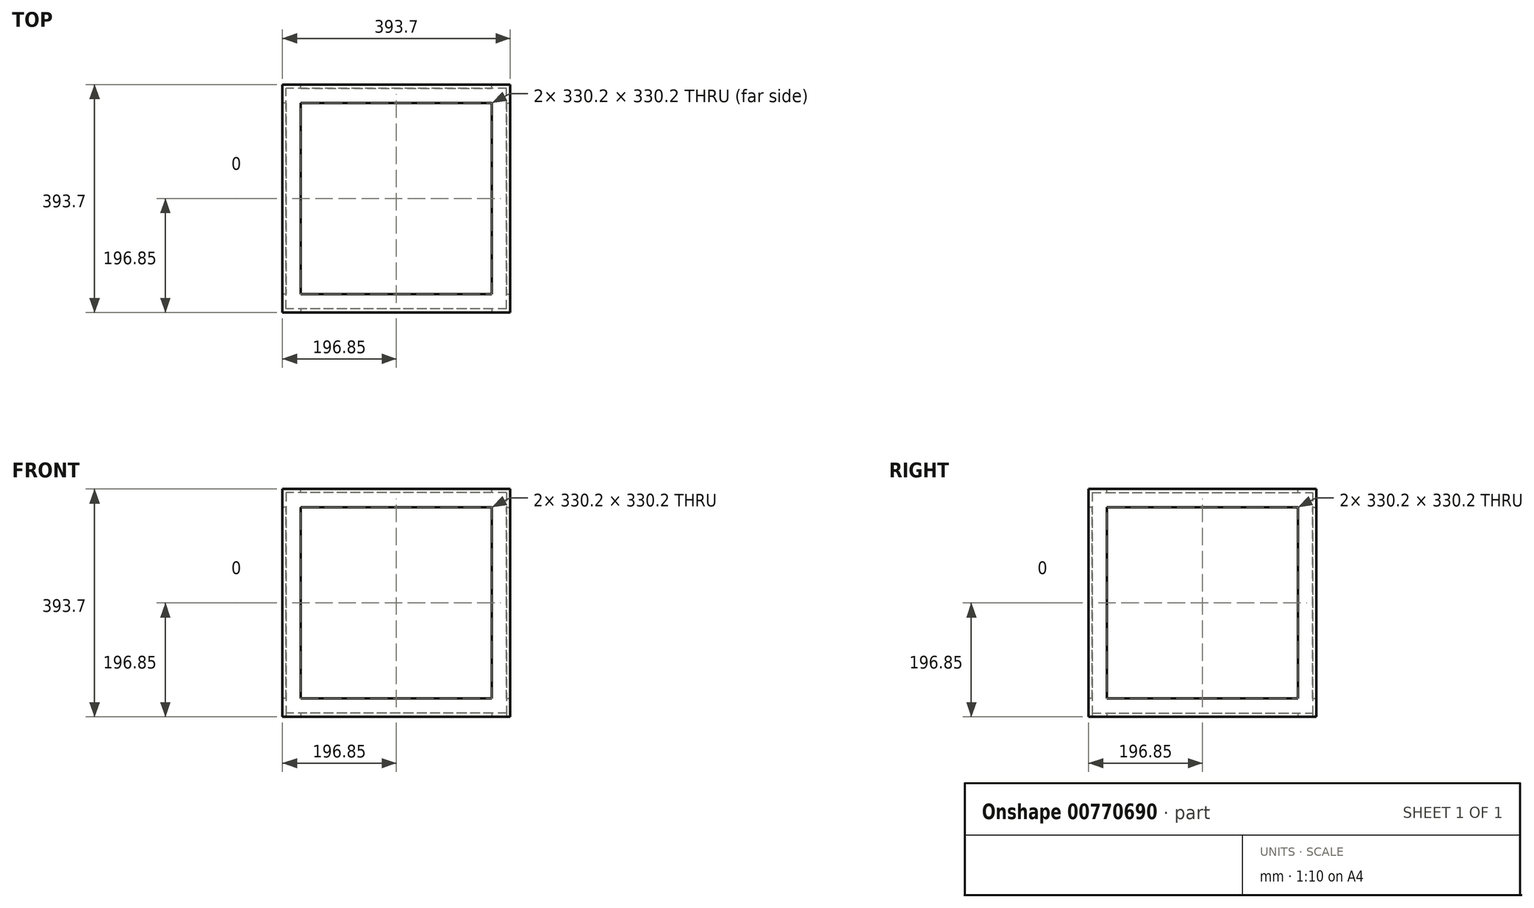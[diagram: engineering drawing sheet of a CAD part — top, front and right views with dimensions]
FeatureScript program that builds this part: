
annotation { "Feature Type Name" : "Feature", "Feature Type Description" : "" }
export const myFeature = defineFeature(function(context is Context, id is Id, definition is map)
    precondition{}
    {
        {
            var Q0;
            Q0=qCreatedBy(makeId("Top.planeOp"),FACE);
            var sketch = newSketch(context, id + "F0", { "sketchPlane" : qUnion([Q0])});
            skLineSegment(sketch, "E0.bottom", {"start": v(190.5, -190.5) * mm, "end": v(-190.5, -190.5) * mm});
            skLineSegment(sketch, "E0.top", {"start": v(190.5, 190.5) * mm, "end": v(-190.5, 190.5) * mm});
            skLineSegment(sketch, "E0.left", {"start": v(190.5, -190.5) * mm, "end": v(190.5, 190.5) * mm});
            skLineSegment(sketch, "E0.right", {"start": v(-190.5, -190.5) * mm, "end": v(-190.5, 190.5) * mm});
            skPoint(sketch, "E0.middle", {"position": v(0, 0) * mm});
            skLineSegment(sketch, "E1.bottom", {"start": v(196.85, -196.85) * mm, "end": v(-196.85, -196.85) * mm});
            skLineSegment(sketch, "E1.top", {"start": v(196.85, 196.85) * mm, "end": v(-196.85, 196.85) * mm});
            skLineSegment(sketch, "E1.left", {"start": v(196.85, -196.85) * mm, "end": v(196.85, 196.85) * mm});
            skLineSegment(sketch, "E1.right", {"start": v(-196.85, -196.85) * mm, "end": v(-196.85, 196.85) * mm});
            skSolve(sketch);
        }
        {
            var Q0;
            Q0 = qSketchRegion(id + "F0", true);
            extrude(context, id + "F1", {"entities" : qUnion([Q0]), "depth" : 393.7 * mm, "offsetDistance" : 25.4 * mm});
        }
        {
            var Q0;
            Q0=makeQuery(id+"F1.opExtrude","SWEPT_FACE",FACE,{"disambiguationData":[OSD([sQuery(id+"F0.wireOp",EDGE,"E1.right")])]});
            var sketch = newSketch(context, id + "F2", { "sketchPlane" : qUnion([Q0])});
            skLineSegment(sketch, "E2.bottom", {"start": v(-165.1, 31.75) * mm, "end": v(165.1, 31.75) * mm});
            skLineSegment(sketch, "E2.top", {"start": v(-165.1, 361.95) * mm, "end": v(165.1, 361.95) * mm});
            skLineSegment(sketch, "E2.left", {"start": v(-165.1, 31.75) * mm, "end": v(-165.1, 361.95) * mm});
            skLineSegment(sketch, "E2.right", {"start": v(165.1, 31.75) * mm, "end": v(165.1, 361.95) * mm});
            skSolve(sketch);
        }
        {
            var Q0;
            Q0 = qSketchRegion(id + "F2", true);
            extrude(context, id + "F3", {"entities" : qUnion([Q0]), "operationType" : NewBodyOperationType.REMOVE, "oppositeDirection" : true, "depth" : 6.35 * mm, "offsetDistance" : 25.4 * mm});
        }
        {
            var Q0;
            Q0=makeQuery(id+"F1.opExtrude","SWEPT_FACE",FACE,{"disambiguationData":[OSD([sQuery(id+"F0.wireOp",EDGE,"E1.top")])]});
            var sketch = newSketch(context, id + "F4", { "sketchPlane" : qUnion([Q0])});
            skLineSegment(sketch, "E3.bottom", {"start": v(165.1, 31.75) * mm, "end": v(-165.1, 31.75) * mm});
            skLineSegment(sketch, "E3.top", {"start": v(165.1, 361.95) * mm, "end": v(-165.1, 361.95) * mm});
            skLineSegment(sketch, "E3.left", {"start": v(165.1, 31.75) * mm, "end": v(165.1, 361.95) * mm});
            skLineSegment(sketch, "E3.right", {"start": v(-165.1, 31.75) * mm, "end": v(-165.1, 361.95) * mm});
            skSolve(sketch);
        }
        {
            var Q0;
            Q0 = qSketchRegion(id + "F4", true);
            extrude(context, id + "F5", {"entities" : qUnion([Q0]), "operationType" : NewBodyOperationType.REMOVE, "oppositeDirection" : true, "depth" : 6.35 * mm, "offsetDistance" : 25.4 * mm});
        }
        {
            var Q0;
            Q0=makeQuery(id+"F1.opExtrude","SWEPT_FACE",FACE,{"disambiguationData":[OSD([sQuery(id+"F0.wireOp",EDGE,"E1.left")])]});
            var sketch = newSketch(context, id + "F6", { "sketchPlane" : qUnion([Q0])});
            skLineSegment(sketch, "E4.bottom", {"start": v(165.1, 31.75) * mm, "end": v(-165.1, 31.75) * mm});
            skLineSegment(sketch, "E4.top", {"start": v(165.1, 361.95) * mm, "end": v(-165.1, 361.95) * mm});
            skLineSegment(sketch, "E4.left", {"start": v(165.1, 31.75) * mm, "end": v(165.1, 361.95) * mm});
            skLineSegment(sketch, "E4.right", {"start": v(-165.1, 31.75) * mm, "end": v(-165.1, 361.95) * mm});
            skSolve(sketch);
        }
        {
            var Q0;
            Q0 = qSketchRegion(id + "F6", true);
            extrude(context, id + "F7", {"entities" : qUnion([Q0]), "operationType" : NewBodyOperationType.REMOVE, "oppositeDirection" : true, "depth" : 6.35 * mm, "offsetDistance" : 25.4 * mm});
        }
        {
            var Q0;
            Q0=makeQuery(id+"F1.opExtrude","SWEPT_FACE",FACE,{"disambiguationData":[OSD([sQuery(id+"F0.wireOp",EDGE,"E1.bottom")])]});
            var sketch = newSketch(context, id + "F8", { "sketchPlane" : qUnion([Q0])});
            skLineSegment(sketch, "E5.bottom", {"start": v(165.1, 31.75) * mm, "end": v(-165.1, 31.75) * mm});
            skLineSegment(sketch, "E5.top", {"start": v(165.1, 361.95) * mm, "end": v(-165.1, 361.95) * mm});
            skLineSegment(sketch, "E5.left", {"start": v(165.1, 31.75) * mm, "end": v(165.1, 361.95) * mm});
            skLineSegment(sketch, "E5.right", {"start": v(-165.1, 31.75) * mm, "end": v(-165.1, 361.95) * mm});
            skSolve(sketch);
        }
        {
            var Q0;
            Q0 = qSketchRegion(id + "F8", true);
            extrude(context, id + "F9", {"entities" : qUnion([Q0]), "operationType" : NewBodyOperationType.REMOVE, "oppositeDirection" : true, "depth" : 6.35 * mm, "offsetDistance" : 25.4 * mm});
        }
        {
            var Q0;
            Q0=makeQuery(id+"F1.opExtrude","CAP_FACE",FACE,{"disambiguationData":[OSD([sQuery(id+"F0.wireOp",EDGE,"E0.bottom"),sQuery(id+"F0.wireOp",EDGE,"E0.top"),sQuery(id+"F0.wireOp",EDGE,"E0.left"),sQuery(id+"F0.wireOp",EDGE,"E0.right"),sQuery(id+"F0.wireOp",EDGE,"E1.bottom"),sQuery(id+"F0.wireOp",EDGE,"E1.top"),sQuery(id+"F0.wireOp",EDGE,"E1.left"),sQuery(id+"F0.wireOp",EDGE,"E1.right")])],"isStart":true});
            var sketch = newSketch(context, id + "F10", { "sketchPlane" : qUnion([Q0])});
            skLineSegment(sketch, "E6.bottom", {"start": v(190.5, -190.5) * mm, "end": v(-190.5, -190.5) * mm});
            skLineSegment(sketch, "E6.top", {"start": v(190.5, 190.5) * mm, "end": v(-190.5, 190.5) * mm});
            skLineSegment(sketch, "E6.left", {"start": v(190.5, -190.5) * mm, "end": v(190.5, 190.5) * mm});
            skLineSegment(sketch, "E6.right", {"start": v(-190.5, -190.5) * mm, "end": v(-190.5, 190.5) * mm});
            skSolve(sketch);
        }
        {
            var Q0;
            Q0 = qSketchRegion(id + "F10", true);
            extrude(context, id + "F11", {"entities" : qUnion([Q0]), "oppositeDirection" : true, "depth" : 6.35 * mm, "offsetDistance" : 25.4 * mm});
        }
        {
            var Q0;
            Q0=makeQuery(id+"F1.opExtrude","CAP_FACE",FACE,{"disambiguationData":[OSD([sQuery(id+"F0.wireOp",EDGE,"E0.bottom"),sQuery(id+"F0.wireOp",EDGE,"E0.top"),sQuery(id+"F0.wireOp",EDGE,"E0.left"),sQuery(id+"F0.wireOp",EDGE,"E0.right"),sQuery(id+"F0.wireOp",EDGE,"E1.bottom"),sQuery(id+"F0.wireOp",EDGE,"E1.top"),sQuery(id+"F0.wireOp",EDGE,"E1.left"),sQuery(id+"F0.wireOp",EDGE,"E1.right")])],"isStart":false});
            var sketch = newSketch(context, id + "F12", { "sketchPlane" : qUnion([Q0])});
            skLineSegment(sketch, "E7.bottom", {"start": v(190.5, -190.5) * mm, "end": v(-196.85, -190.5) * mm});
            skLineSegment(sketch, "E7.top", {"start": v(190.5, 196.85) * mm, "end": v(-196.85, 196.85) * mm});
            skLineSegment(sketch, "E7.left", {"start": v(190.5, -190.5) * mm, "end": v(190.5, 196.85) * mm});
            skLineSegment(sketch, "E7.right", {"start": v(-196.85, -190.5) * mm, "end": v(-196.85, 196.85) * mm});
            skSolve(sketch);
        }
        {
            var Q0;
            Q0 = qSketchRegion(id + "F12", true);
            extrude(context, id + "F13", {"entities" : qUnion([Q0]), "operationType" : NewBodyOperationType.ADD, "oppositeDirection" : true, "depth" : 6.35 * mm, "offsetDistance" : 25.4 * mm});
        }
        {
            var Q0;
            Q0=makeQuery(id+"F11.opExtrude","CAP_FACE",FACE,{"disambiguationData":[OSD([sQuery(id+"F10.wireOp",EDGE,"E6.bottom"),sQuery(id+"F10.wireOp",EDGE,"E6.top"),sQuery(id+"F10.wireOp",EDGE,"E6.left"),sQuery(id+"F10.wireOp",EDGE,"E6.right")])],"isStart":true});
            var sketch = newSketch(context, id + "F14", { "sketchPlane" : qUnion([Q0])});
            skLineSegment(sketch, "E8.bottom", {"start": v(165.1, 165.1) * mm, "end": v(-165.1, 165.1) * mm});
            skLineSegment(sketch, "E8.top", {"start": v(165.1, -165.1) * mm, "end": v(-165.1, -165.1) * mm});
            skLineSegment(sketch, "E8.left", {"start": v(165.1, 165.1) * mm, "end": v(165.1, -165.1) * mm});
            skLineSegment(sketch, "E8.right", {"start": v(-165.1, 165.1) * mm, "end": v(-165.1, -165.1) * mm});
            skSolve(sketch);
        }
        {
            var Q0;
            Q0 = qSketchRegion(id + "F14", true);
            extrude(context, id + "F15", {"entities" : qUnion([Q0]), "operationType" : NewBodyOperationType.REMOVE, "oppositeDirection" : true, "depth" : 6.35 * mm, "offsetDistance" : 25.4 * mm});
        }
        {
            var Q0;
            Q0=makeQuery(id+"F13.boolean.opBoolean","MERGE",FACE,{"derivedFrom":[makeQuery(id+"F1.opExtrude","CAP_FACE",FACE,{"disambiguationData":[OSD([sQuery(id+"F0.wireOp",EDGE,"E0.bottom"),sQuery(id+"F0.wireOp",EDGE,"E0.top"),sQuery(id+"F0.wireOp",EDGE,"E0.left"),sQuery(id+"F0.wireOp",EDGE,"E0.right"),sQuery(id+"F0.wireOp",EDGE,"E1.bottom"),sQuery(id+"F0.wireOp",EDGE,"E1.top"),sQuery(id+"F0.wireOp",EDGE,"E1.left"),sQuery(id+"F0.wireOp",EDGE,"E1.right")])],"isStart":false}),makeQuery(id+"F13.opExtrude","CAP_FACE",FACE,{"disambiguationData":[OSD([sQuery(id+"F12.wireOp",EDGE,"E7.bottom"),sQuery(id+"F12.wireOp",EDGE,"E7.top"),sQuery(id+"F12.wireOp",EDGE,"E7.left"),sQuery(id+"F12.wireOp",EDGE,"E7.right")])],"isStart":true})]});
            var sketch = newSketch(context, id + "F16", { "sketchPlane" : qUnion([Q0])});
            skLineSegment(sketch, "E9.bottom", {"start": v(165.1, -165.1) * mm, "end": v(-165.1, -165.1) * mm});
            skLineSegment(sketch, "E9.top", {"start": v(165.1, 165.1) * mm, "end": v(-165.1, 165.1) * mm});
            skLineSegment(sketch, "E9.left", {"start": v(165.1, -165.1) * mm, "end": v(165.1, 165.1) * mm});
            skLineSegment(sketch, "E9.right", {"start": v(-165.1, -165.1) * mm, "end": v(-165.1, 165.1) * mm});
            skSolve(sketch);
        }
        {
            var Q0;
            Q0 = qSketchRegion(id + "F16", true);
            extrude(context, id + "F17", {"entities" : qUnion([Q0]), "operationType" : NewBodyOperationType.REMOVE, "oppositeDirection" : true, "depth" : 6.35 * mm, "offsetDistance" : 25.4 * mm});
        }
    });
